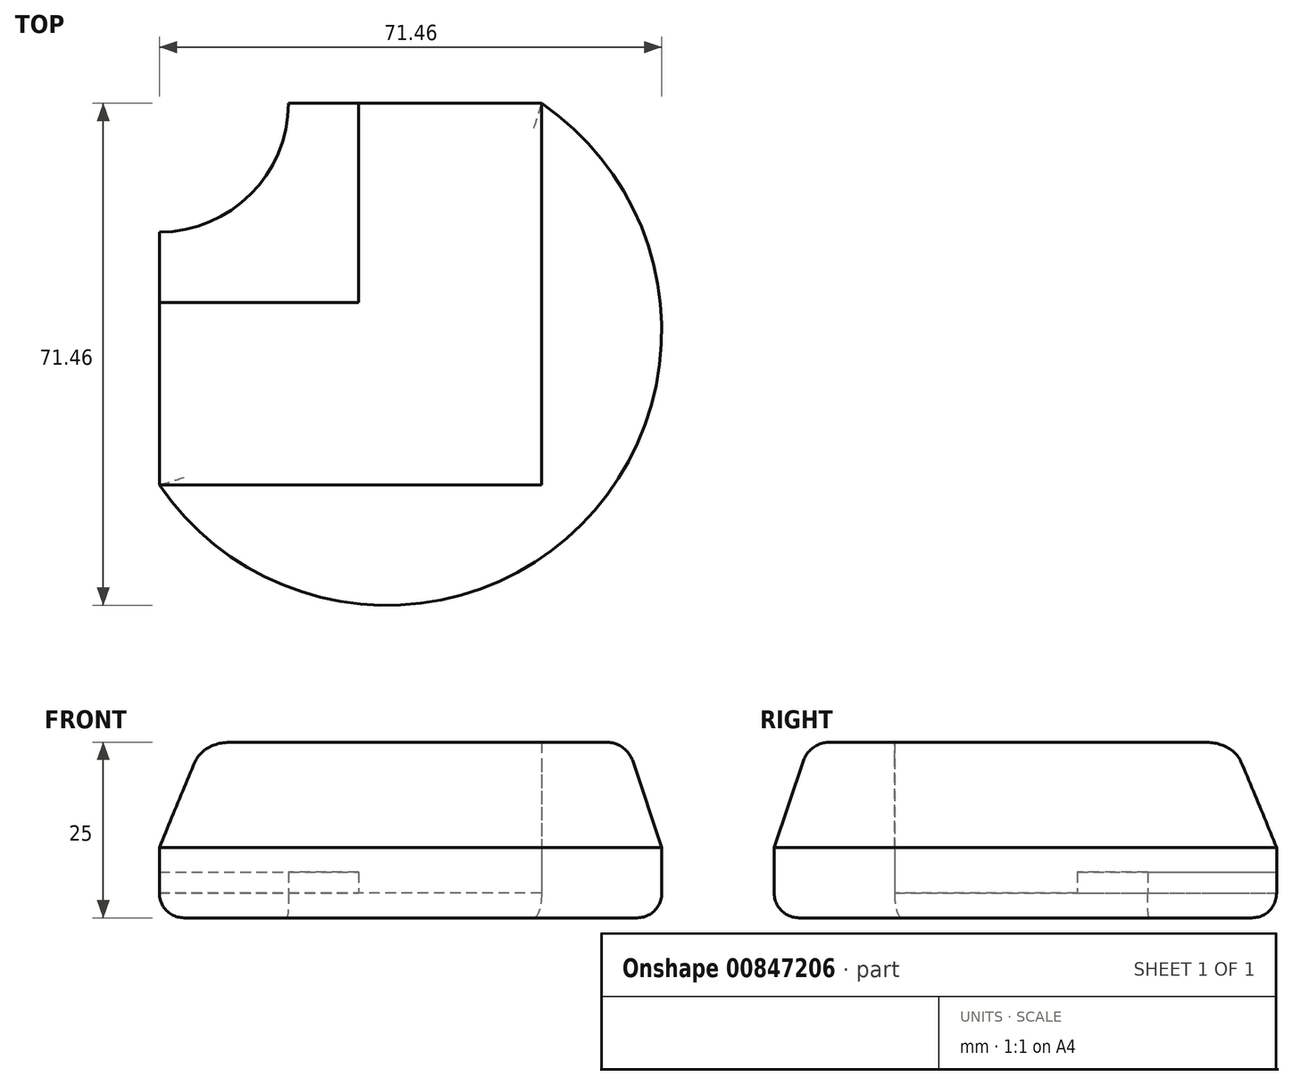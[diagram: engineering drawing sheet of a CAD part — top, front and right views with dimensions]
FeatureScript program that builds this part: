
annotation { "Feature Type Name" : "Feature", "Feature Type Description" : "" }
export const myFeature = defineFeature(function(context is Context, id is Id, definition is map)
    precondition{}
    {
        {
            var Q0;
            Q0=qCreatedBy(makeId("Top.planeOp"),FACE);
            var sketch = newSketch(context, id + "F0", { "sketchPlane" : qUnion([Q0])});
            skLineSegment(sketch, "E0.bottom", {"start": v(24.34, 30) * mm, "end": v(-11.66, 30) * mm});
            skLineSegment(sketch, "E0.right", {"start": v(-30, 11.66) * mm, "end": v(-30, -24.34) * mm});
            skPoint(sketch, "E0.middle", {"position": v(0, 0) * mm});
            skLineSegment(sketch, "E1", {"start": v(24.34, -24.34) * mm, "end": v(24.34, 30) * mm});
            skLineSegment(sketch, "E2", {"start": v(24.34, -24.34) * mm, "end": v(-30, -24.34) * mm});
            skLineSegment(sketch, "E3", {"start": v(-30, 1.66) * mm, "end": v(-1.66, 1.66) * mm});
            skLineSegment(sketch, "E4", {"start": v(-1.66, 1.66) * mm, "end": v(-1.66, 30) * mm});
            skPoint(sketch, "E5", {"position": v(-30, 11.66) * mm});
            skPoint(sketch, "E6", {"position": v(-11.66, 30) * mm});
            skArc(sketch, "E7", {"start": v(-30, 11.66) * mm, "mid": v(-17.05, 17.05) * mm, "end": v(-11.66, 30) * mm});
            skArc(sketch, "E8", {"start": v(-30, -24.34) * mm, "mid": v(30, -30) * mm, "end": v(24.34, 30) * mm});
            skSolve(sketch);
        }
        {
            var Q0;
            {var subQ1=sQuery(id+"F0.wireOp",EDGE,"E3");Q0=makeQuery(id+"F0.imprint","IMPRINT",FACE,{"disambiguationData":[TD([[makeQuery(id+"F0.imprint","IMPRINT",EDGE,{"derivedFrom":subQ1}),1.0]])]});}
            extrude(context, id + "F1", {"entities" : qUnion([Q0]), "depth" : 6.5 * mm, "offsetDistance" : 25 * mm});
        }
        {
            var Q0;
            {var subQ1=sQuery(id+"F0.wireOp",EDGE,"E1");Q0=makeQuery(id+"F0.imprint","IMPRINT",FACE,{"disambiguationData":[TD([[makeQuery(id+"F0.imprint","IMPRINT",EDGE,{"derivedFrom":subQ1}),1.0]])]});}
            extrude(context, id + "F2", {"entities" : qUnion([Q0]), "operationType" : NewBodyOperationType.ADD, "depth" : 3.5 * mm, "offsetDistance" : 25 * mm});
        }
        {
            var Q0;
            Q0=makeQuery(id+"F0.imprint","IMPRINT",FACE,{"disambiguationData":[TD([[makeQuery(id+"F0.imprint","IMPRINT",EDGE,{"derivedFrom":sQuery(id+"F0.wireOp",EDGE,"E1")}),-1.0]])]});
            extrude(context, id + "F3", {"entities" : qUnion([Q0]), "operationType" : NewBodyOperationType.ADD, "depth" : 25 * mm, "offsetDistance" : 25 * mm});
        }
        {
            var Q0;
            Q0=makeQuery(id+"F3.opExtrude","CAP_EDGE",EDGE,{"disambiguationData":[OSD([sQuery(id+"F0.wireOp",EDGE,"E8")])],"isStart":true});
            var Q1;
            {var subQ0=sQuery(id+"F0.wireOp",EDGE,"E0.right");Q1=makeQuery(id+"F2.boolean.opBoolean","MERGE",EDGE,{"derivedFrom":[makeQuery(id+"F1.opExtrude","CAP_EDGE",EDGE,{"disambiguationData":[OSD([subQ0])],"isStart":true}),makeQuery(id+"F2.opExtrude","CAP_EDGE",EDGE,{"disambiguationData":[OSD([subQ0])],"isStart":true})]});}
            var Q2;
            {var subQ0=sQuery(id+"F0.wireOp",EDGE,"E0.bottom");Q2=makeQuery(id+"F2.boolean.opBoolean","MERGE",EDGE,{"derivedFrom":[makeQuery(id+"F1.opExtrude","CAP_EDGE",EDGE,{"disambiguationData":[OSD([subQ0])],"isStart":true}),makeQuery(id+"F2.opExtrude","CAP_EDGE",EDGE,{"disambiguationData":[OSD([subQ0])],"isStart":true})]});}
            fillet(context, id + "F4", {"entities" : qUnion([Q0, Q1, Q2]), "radius" : 3.5 * mm, "tangentPropagation" : true, "allowEdgeOverflow" : false});
        }
        {
            var Q0;
            Q0=makeQuery(id+"F3.opExtrude","CAP_EDGE",EDGE,{"disambiguationData":[OSD([sQuery(id+"F0.wireOp",EDGE,"E8")])],"isStart":false});
            chamfer(context, id + "F5", {"entities" : qUnion([Q0]), "chamferType" : ChamferType.TWO_OFFSETS, "width1" : 5 * mm, "oppositeDirection" : false, "width2" : 15 * mm, "tangentPropagation" : true});
        }
        {
            var Q0;
            {var subQ0=sQuery(id+"F0.wireOp",EDGE,"E8");Q0=makeQuery(id+"F5.opChamfer","BLEND_EDGE",EDGE,{"blendedFrom":[makeQuery(id+"F3.opExtrude","CAP_EDGE",EDGE,{"disambiguationData":[OSD([subQ0])],"isStart":false}),makeQuery(id+"F3.opExtrude","CAP_FACE",FACE,{"disambiguationData":[OSD([sQuery(id+"F0.wireOp",EDGE,"E1"),sQuery(id+"F0.wireOp",EDGE,"E2"),subQ0])],"isStart":false})],"blendedInto":[makeQuery(id+"F3.opExtrude","CAP_FACE",FACE,{"disambiguationData":[OSD([sQuery(id+"F0.wireOp",EDGE,"E1"),sQuery(id+"F0.wireOp",EDGE,"E2"),subQ0])],"isStart":false})]});}
            fillet(context, id + "F6", {"entities" : qUnion([Q0]), "radius" : 4 * mm, "tangentPropagation" : true, "allowEdgeOverflow" : false});
        }
    });
